# Revit family: STL22451BR_STL22451PTO
name_source: partatom
category: Luminárias
units: mm (PartAtom-declared; Revit-internal decimal feet)

## family parameters
Com base no plano de trabalho = Não
Compartilhado = Não
Corte com vazios quando carregada = Não
Cota do conector redondo = Utilizar diâmetro
Fonte luminosa = Não
Manter orientação da anotação = Não
Número OmniClass = 23.80.70.00
Ponto de cálculo do ambiente = Não
Sempre na vertical = Sim
Tipo de parte = Normal
Título OmniClass = Lighting

## types (2) — shared parameters
Acabamento Spot = Al - Preto
Fabricante = Stella
Grau de proteção (IP) = IP20
Modelo = Flow MR11 para Trace
Potência máxima = 15 W
Tensão Elétrica = 127-220V
URL = https://stella.com.br
zero-valued in all types: Altura do Spot, Comprimento do Spot, Diâmetro do Spot, Elevação padrão

## per-type parameters (varying)
| type | Estrutura | Referência |
| STL22451PTO/30 - PRETO | Al - Preto | STL22451PTO/30 |
| STL22451BR/30 - BRANCO | Al - Branco | STL22451BR/30 |
